# Revit family: Legrand_Practibox³_8_et_12_modules_porte_transparente
name_source: partatom
category: Equipement électrique
revit_build: Autodesk Revit 2018 (Build: 20170223_1515(x64)
units: mm (PartAtom-declared; Revit-internal decimal feet)

## family parameters
Basée sur le plan de construction = Non
Configuration du panneau = Deux colonnes, circuits au sein
Cote de connecteur circulaire = Utiliser le diamètre
Couper avec des vides une fois chargée = Non
Numéro OmniClass = 23.80.30.11.17
Partagée = Non
Point de calcul de pièce = Non
Titre OmniClass = Distribution Boards and Control Panels
Toujours verticalement = Oui
Type d'élément = Tableau de raccordement

## types (8) — shared parameters
Conditions Générale d'Utilisation = https://export.legrand.com
Fabricant = Legrand
Modèle = Practibox³
URL = www.legrand.com
porte blanche = Non
porte transparente = Oui

## per-type parameters (varying)
| type | 401701 | 401702 | 401703 | 401704 | 401751 | 401752 | 401753 | 401754 | Bornier N | Bornier T | Hauteur | Largeur | profondeur |
| Practibox³ 1x8 modules 401701 | Oui | Non | Non | Non | Non | Non | Non | Non |  | Bornier 8 trous | 208 mm  [stored 0.682415 ft] | 286 mm | 100 mm  [stored 0.328084 ft] |
| Practibox³ 1x12 modules 401702 | Non | Oui | Non | Non | Non | Non | Non | Non |  | Bornier 13 trous | 246 mm  [stored 0.807087 ft] | 359 mm  [stored 1.17782 ft] | 100 mm  [stored 0.328084 ft] |
| Practibox³ 2x12 modules 401703 | Non | Non | Oui | Non | Non | Non | Non | Non |  | Bornier 17 trous | 396 mm  [stored 1.29921 ft] | 359 mm  [stored 1.17782 ft] | 105 mm  [stored 0.344488 ft] |
| Practibox³ 3x12 modules 401704 | Non | Non | Non | Oui | Non | Non | Non | Non |  | Bornier 22 trous | 546 mm  [stored 1.79134 ft] | 359 mm  [stored 1.17782 ft] | 105 mm  [stored 0.344488 ft] |
| Practibox³ 1x8 modules 401751 | Non | Non | Non | Non | Oui | Non | Non | Non | Bornier 8 trous | Bornier 8 trous | 208 mm  [stored 0.682415 ft] | 286 mm | 100 mm  [stored 0.328084 ft] |
| Practibox³ 1x12 modules 401752 | Non | Non | Non | Non | Non | Oui | Non | Non | Bornier 8 trous | Bornier 13 trous | 246 mm  [stored 0.807087 ft] | 359 mm  [stored 1.17782 ft] | 100 mm  [stored 0.328084 ft] |
| Practibox³ 2x12 modules 401753 | Non | Non | Non | Non | Non | Non | Oui | Non | bornier 2x8 trous | Bornier 17 trous | 396 mm  [stored 1.29921 ft] | 359 mm  [stored 1.17782 ft] | 105 mm  [stored 0.344488 ft] |
| Practibox³ 3x12 modules 401754 | Non | Non | Non | Non | Non | Non | Non | Oui | bornier 3x8 trous | Bornier 22 trous | 546 mm  [stored 1.79134 ft] | 359 mm  [stored 1.17782 ft] | 105 mm  [stored 0.344488 ft] |

note: [stored X ft] marks values corroborated as IEEE doubles in the binary element streams (Revit-internal decimal feet)
